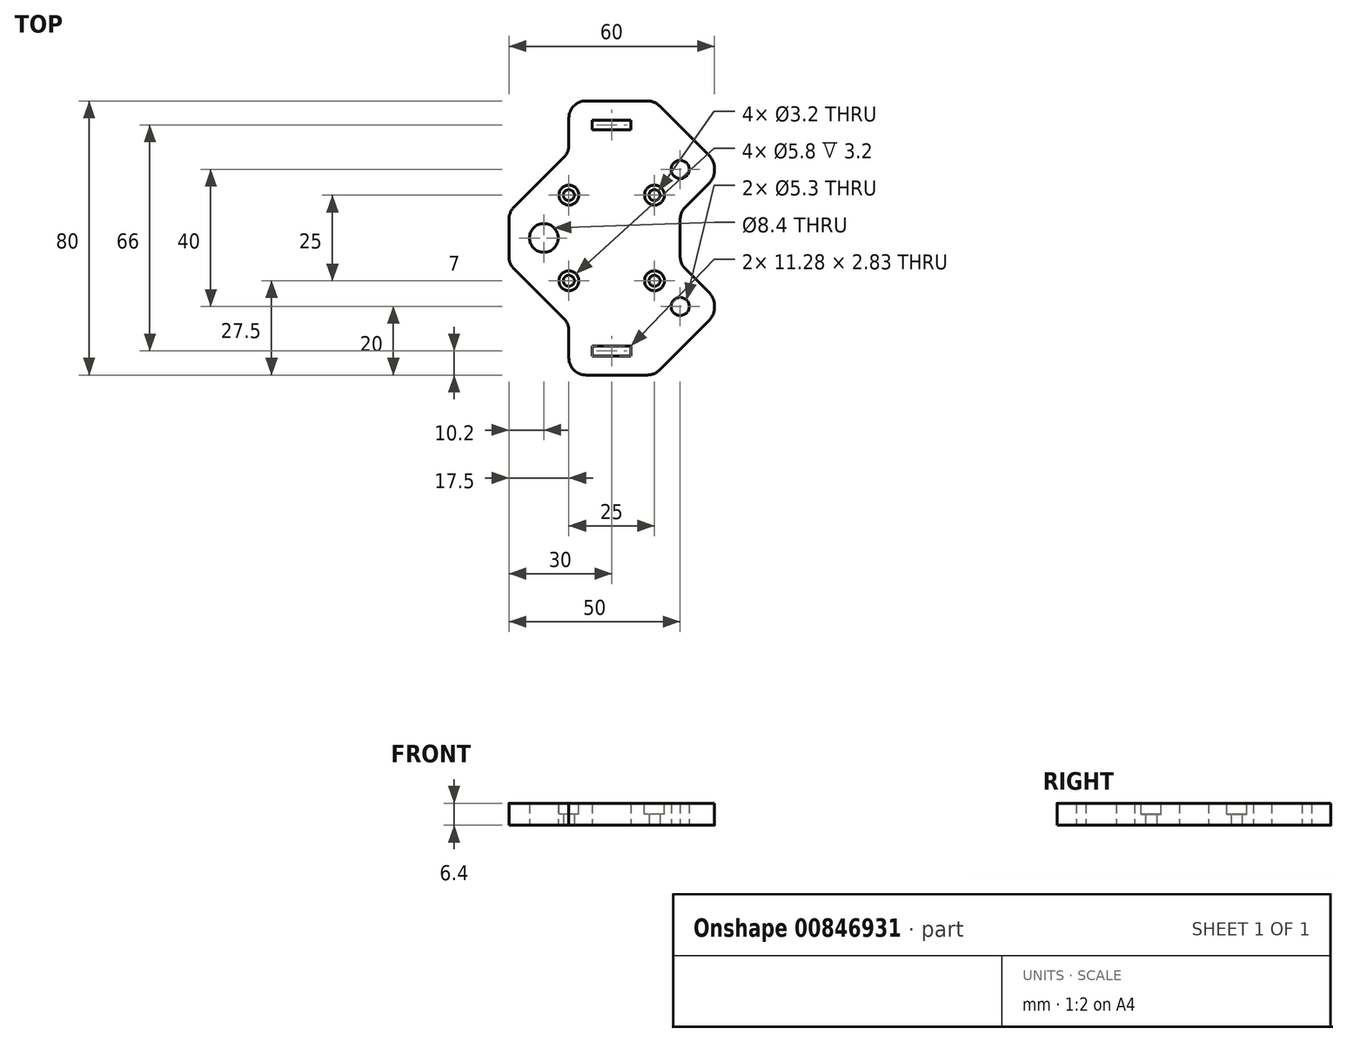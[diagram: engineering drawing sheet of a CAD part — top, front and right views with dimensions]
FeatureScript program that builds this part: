
annotation { "Feature Type Name" : "Feature", "Feature Type Description" : "" }
export const myFeature = defineFeature(function(context is Context, id is Id, definition is map)
    precondition{}
    {
        {
            var Q0;
            Q0=qCreatedBy(makeId("Top.planeOp"),FACE);
            var sketch = newSketch(context, id + "F0", { "sketchPlane" : qUnion([Q0])});
            skLineSegment(sketch, "E0.bottom", {"start": v(12.5, -40) * mm, "end": v(-12.5, -40) * mm});
            skLineSegment(sketch, "E0.top", {"start": v(12.5, 40) * mm, "end": v(-12.5, 40) * mm});
            skLineSegment(sketch, "E0.left", {"start": v(30, -22.5) * mm, "end": v(30, -17.5) * mm});
            skLineSegment(sketch, "E0.right", {"start": v(-30, -7.5) * mm, "end": v(-30, 7.5) * mm});
            skPoint(sketch, "E0.middle", {"position": v(0, 0) * mm});
            skLineSegment(sketch, "E1.bottom", {"start": v(12.5, -12.5) * mm, "end": v(-12.5, -12.5) * mm, "construction": true});
            skLineSegment(sketch, "E1.top", {"start": v(12.5, 12.5) * mm, "end": v(-12.5, 12.5) * mm, "construction": true});
            skLineSegment(sketch, "E1.left", {"start": v(12.5, -12.5) * mm, "end": v(12.5, 12.5) * mm, "construction": true});
            skLineSegment(sketch, "E1.right", {"start": v(-12.5, -12.5) * mm, "end": v(-12.5, 12.5) * mm, "construction": true});
            skCircle(sketch, "E2", {"center": v(-12.5, 12.5) * mm, "radius": 1.6 * mm});
            skCircle(sketch, "E3", {"center": v(12.5, 12.5) * mm, "radius": 1.6 * mm});
            skCircle(sketch, "E4", {"center": v(12.5, -12.5) * mm, "radius": 1.6 * mm});
            skCircle(sketch, "E5", {"center": v(-12.5, -12.5) * mm, "radius": 1.6 * mm});
            skCircle(sketch, "E6", {"center": v(20, 20) * mm, "radius": 2.65 * mm});
            skCircle(sketch, "E7", {"center": v(20, -20) * mm, "radius": 2.65 * mm});
            skCircle(sketch, "E8", {"center": v(-19.8, 0) * mm, "radius": 4.2 * mm});
            skLineSegment(sketch, "E9", {"start": v(0, 0) * mm, "end": v(30, 0) * mm, "construction": true});
            skLineSegment(sketch, "E10", {"start": v(20, 20) * mm, "end": v(20, 0) * mm, "construction": true});
            skLineSegment(sketch, "E11.bottom", {"start": v(5.64, 31.59) * mm, "end": v(-5.64, 31.59) * mm});
            skLineSegment(sketch, "E11.top", {"start": v(5.64, 34.41) * mm, "end": v(-5.64, 34.41) * mm});
            skLineSegment(sketch, "E11.left", {"start": v(5.64, 31.59) * mm, "end": v(5.64, 34.41) * mm});
            skLineSegment(sketch, "E11.right", {"start": v(-5.64, 31.59) * mm, "end": v(-5.64, 34.41) * mm});
            skPoint(sketch, "E11.middle", {"position": v(0, 33) * mm});
            skLineSegment(sketch, "E12.bottom", {"start": v(5.64, -34.41) * mm, "end": v(-5.64, -34.41) * mm});
            skLineSegment(sketch, "E12.top", {"start": v(5.64, -31.59) * mm, "end": v(-5.64, -31.59) * mm});
            skLineSegment(sketch, "E12.left", {"start": v(5.64, -34.41) * mm, "end": v(5.64, -31.59) * mm});
            skLineSegment(sketch, "E12.right", {"start": v(-5.64, -34.41) * mm, "end": v(-5.64, -31.59) * mm});
            skPoint(sketch, "E12.middle", {"position": v(0, -33) * mm});
            skLineSegment(sketch, "E13", {"start": v(-30, 7.5) * mm, "end": v(-12.5, 25) * mm});
            skLineSegment(sketch, "E14", {"start": v(-30, -7.5) * mm, "end": v(-12.5, -25) * mm});
            skLineSegment(sketch, "E15", {"start": v(12.5, -40) * mm, "end": v(30, -22.5) * mm});
            skLineSegment(sketch, "E16", {"start": v(12.5, 40) * mm, "end": v(30, 22.5) * mm});
            skLineSegment(sketch, "E17", {"start": v(0, 0) * mm, "end": v(0, 40) * mm, "construction": true});
            skLineSegment(sketch, "E18", {"start": v(30, 17.5) * mm, "end": v(20, 7.5) * mm});
            skLineSegment(sketch, "E19", {"start": v(20, -7.5) * mm, "end": v(30, -17.5) * mm});
            skLineSegment(sketch, "E20.trimOffspring", {"start": v(30, 17.5) * mm, "end": v(30, 22.5) * mm});
            skLineSegment(sketch, "E21", {"start": v(-12.5, -40) * mm, "end": v(-12.5, -25) * mm});
            skLineSegment(sketch, "E22", {"start": v(-12.5, 25) * mm, "end": v(-12.5, 40) * mm});
            skPoint(sketch, "E23", {"position": v(-30, 0) * mm});
            skLineSegment(sketch, "E24", {"start": v(20, -7.5) * mm, "end": v(20, 7.5) * mm});
            skPoint(sketch, "E25", {"position": v(30, -20) * mm});
            skSolve(sketch);
        }
        {
            var Q0;
            Q0 = qSketchRegion(id + "F0", true);
            extrude(context, id + "F1", {"entities" : qUnion([Q0]), "depth" : 6.4 * mm, "offsetDistance" : 25 * mm});
        }
        {
            var Q0;
            Q0=makeQuery(id+"F1.opExtrude","SWEPT_EDGE",EDGE,{"disambiguationData":[OSD([sQuery(id+"F0.wireOp",EDGE,"E0.top"),sQuery(id+"F0.wireOp",EDGE,"E0.right")])]});
            var Q1;
            Q1=makeQuery(id+"F1.opExtrude","SWEPT_EDGE",EDGE,{"disambiguationData":[OSD([sQuery(id+"F0.wireOp",EDGE,"E0.top"),sQuery(id+"F0.wireOp",EDGE,"E0.left")])]});
            var Q2;
            Q2=makeQuery(id+"F1.opExtrude","SWEPT_EDGE",EDGE,{"disambiguationData":[OSD([sQuery(id+"F0.wireOp",EDGE,"E0.bottom"),sQuery(id+"F0.wireOp",EDGE,"E0.left")])]});
            var Q3;
            Q3=makeQuery(id+"F1.opExtrude","SWEPT_EDGE",EDGE,{"disambiguationData":[OSD([sQuery(id+"F0.wireOp",EDGE,"E0.bottom"),sQuery(id+"F0.wireOp",EDGE,"E0.right")])]});
            var Q4;
            Q4=makeQuery(id+"F1.opExtrude","SWEPT_EDGE",EDGE,{"disambiguationData":[OSD([sQuery(id+"F0.wireOp",EDGE,"E18"),sQuery(id+"F0.wireOp",EDGE,"E20.trimOffspring")])]});
            var Q5;
            Q5=makeQuery(id+"F1.opExtrude","SWEPT_EDGE",EDGE,{"disambiguationData":[OSD([sQuery(id+"F0.wireOp",EDGE,"E16"),sQuery(id+"F0.wireOp",EDGE,"E20.trimOffspring")])]});
            var Q6;
            Q6=makeQuery(id+"F1.opExtrude","SWEPT_EDGE",EDGE,{"disambiguationData":[OSD([sQuery(id+"F0.wireOp",EDGE,"E18"),sQuery(id+"F0.wireOp",EDGE,"E19")])]});
            var Q7;
            Q7=makeQuery(id+"F1.opExtrude","SWEPT_EDGE",EDGE,{"disambiguationData":[OSD([sQuery(id+"F0.wireOp",EDGE,"o4pbFCMn-Cgn1-SrJc-Cifb-GgxK6Z8VvsFo.top"),sQuery(id+"F0.wireOp",EDGE,"o4pbFCMn-Cgn1-SrJc-Cifb-GgxK6Z8VvsFo.right")])]});
            var Q8;
            Q8=makeQuery(id+"F1.opExtrude","SWEPT_EDGE",EDGE,{"disambiguationData":[OSD([sQuery(id+"F0.wireOp",EDGE,"o4pbFCMn-Cgn1-SrJc-Cifb-GgxK6Z8VvsFo.top"),sQuery(id+"F0.wireOp",EDGE,"o4pbFCMn-Cgn1-SrJc-Cifb-GgxK6Z8VvsFo.left")])]});
            var Q9;
            Q9=makeQuery(id+"F1.opExtrude","SWEPT_EDGE",EDGE,{"disambiguationData":[OSD([sQuery(id+"F0.wireOp",EDGE,"o4pbFCMn-Cgn1-SrJc-Cifb-GgxK6Z8VvsFo.bottom"),sQuery(id+"F0.wireOp",EDGE,"o4pbFCMn-Cgn1-SrJc-Cifb-GgxK6Z8VvsFo.left")])]});
            var Q10;
            Q10=makeQuery(id+"F1.opExtrude","SWEPT_EDGE",EDGE,{"disambiguationData":[OSD([sQuery(id+"F0.wireOp",EDGE,"o4pbFCMn-Cgn1-SrJc-Cifb-GgxK6Z8VvsFo.bottom"),sQuery(id+"F0.wireOp",EDGE,"o4pbFCMn-Cgn1-SrJc-Cifb-GgxK6Z8VvsFo.right")])]});
            var Q11;
            Q11=makeQuery(id+"F1.opExtrude","SWEPT_EDGE",EDGE,{"disambiguationData":[OSD([sQuery(id+"F0.wireOp",EDGE,"E14"),sQuery(id+"F0.wireOp",EDGE,"E21")])]});
            var Q12;
            Q12=makeQuery(id+"F1.opExtrude","SWEPT_EDGE",EDGE,{"disambiguationData":[OSD([sQuery(id+"F0.wireOp",EDGE,"E13"),sQuery(id+"F0.wireOp",EDGE,"E22")])]});
            fillet(context, id + "F2", {"entities" : qUnion([Q0, Q1, Q2, Q3, Q4, Q5, Q6, Q7, Q8, Q9, Q10, Q11, Q12]), "radius" : 5 * mm, "tangentPropagation" : true, "allowEdgeOverflow" : false});
        }
        {
            var Q0;
            Q0=makeQuery(id+"F1.opExtrude","CAP_FACE",FACE,{"disambiguationData":[OSD([sQuery(id+"F0.wireOp",EDGE,"E0.bottom"),sQuery(id+"F0.wireOp",EDGE,"E0.top"),sQuery(id+"F0.wireOp",EDGE,"E0.left"),sQuery(id+"F0.wireOp",EDGE,"E0.right"),sQuery(id+"F0.wireOp",EDGE,"E2"),sQuery(id+"F0.wireOp",EDGE,"E3"),sQuery(id+"F0.wireOp",EDGE,"E4"),sQuery(id+"F0.wireOp",EDGE,"E5"),sQuery(id+"F0.wireOp",EDGE,"E6"),sQuery(id+"F0.wireOp",EDGE,"E7"),sQuery(id+"F0.wireOp",EDGE,"E8"),sQuery(id+"F0.wireOp",EDGE,"E11.bottom"),sQuery(id+"F0.wireOp",EDGE,"E11.top"),sQuery(id+"F0.wireOp",EDGE,"E11.left"),sQuery(id+"F0.wireOp",EDGE,"E11.right"),sQuery(id+"F0.wireOp",EDGE,"E12.bottom"),sQuery(id+"F0.wireOp",EDGE,"E12.top"),sQuery(id+"F0.wireOp",EDGE,"E12.left"),sQuery(id+"F0.wireOp",EDGE,"E12.right"),sQuery(id+"F0.wireOp",EDGE,"E13"),sQuery(id+"F0.wireOp",EDGE,"E14"),sQuery(id+"F0.wireOp",EDGE,"E15"),sQuery(id+"F0.wireOp",EDGE,"E16"),sQuery(id+"F0.wireOp",EDGE,"E18"),sQuery(id+"F0.wireOp",EDGE,"E19"),sQuery(id+"F0.wireOp",EDGE,"E20.trimOffspring"),sQuery(id+"F0.wireOp",EDGE,"E21"),sQuery(id+"F0.wireOp",EDGE,"E22"),sQuery(id+"F0.wireOp",EDGE,"E24")])],"isStart":false});
            var sketch = newSketch(context, id + "F3", { "sketchPlane" : qUnion([Q0])});
            skCircle(sketch, "E26.0", {"center": v(-12.5, 12.5) * mm, "radius": 1.6 * mm, "construction": true});
            skCircle(sketch, "E27.0", {"center": v(-12.5, -12.5) * mm, "radius": 1.6 * mm, "construction": true});
            skCircle(sketch, "E28.0", {"center": v(12.5, -12.5) * mm, "radius": 1.6 * mm, "construction": true});
            skCircle(sketch, "E29.0", {"center": v(12.5, 12.5) * mm, "radius": 1.6 * mm, "construction": true});
            skCircle(sketch, "E30", {"center": v(-12.5, 12.5) * mm, "radius": 2.9 * mm});
            skCircle(sketch, "E31", {"center": v(12.5, 12.5) * mm, "radius": 2.9 * mm});
            skCircle(sketch, "E32", {"center": v(12.5, -12.5) * mm, "radius": 2.9 * mm});
            skCircle(sketch, "E33", {"center": v(-12.5, -12.5) * mm, "radius": 2.9 * mm});
            skSolve(sketch);
        }
        {
            var Q0;
            Q0 = qSketchRegion(id + "F3", true);
            extrude(context, id + "F4", {"entities" : qUnion([Q0]), "operationType" : NewBodyOperationType.REMOVE, "oppositeDirection" : true, "depth" : 3.2 * mm, "offsetDistance" : 25 * mm});
        }
    });
